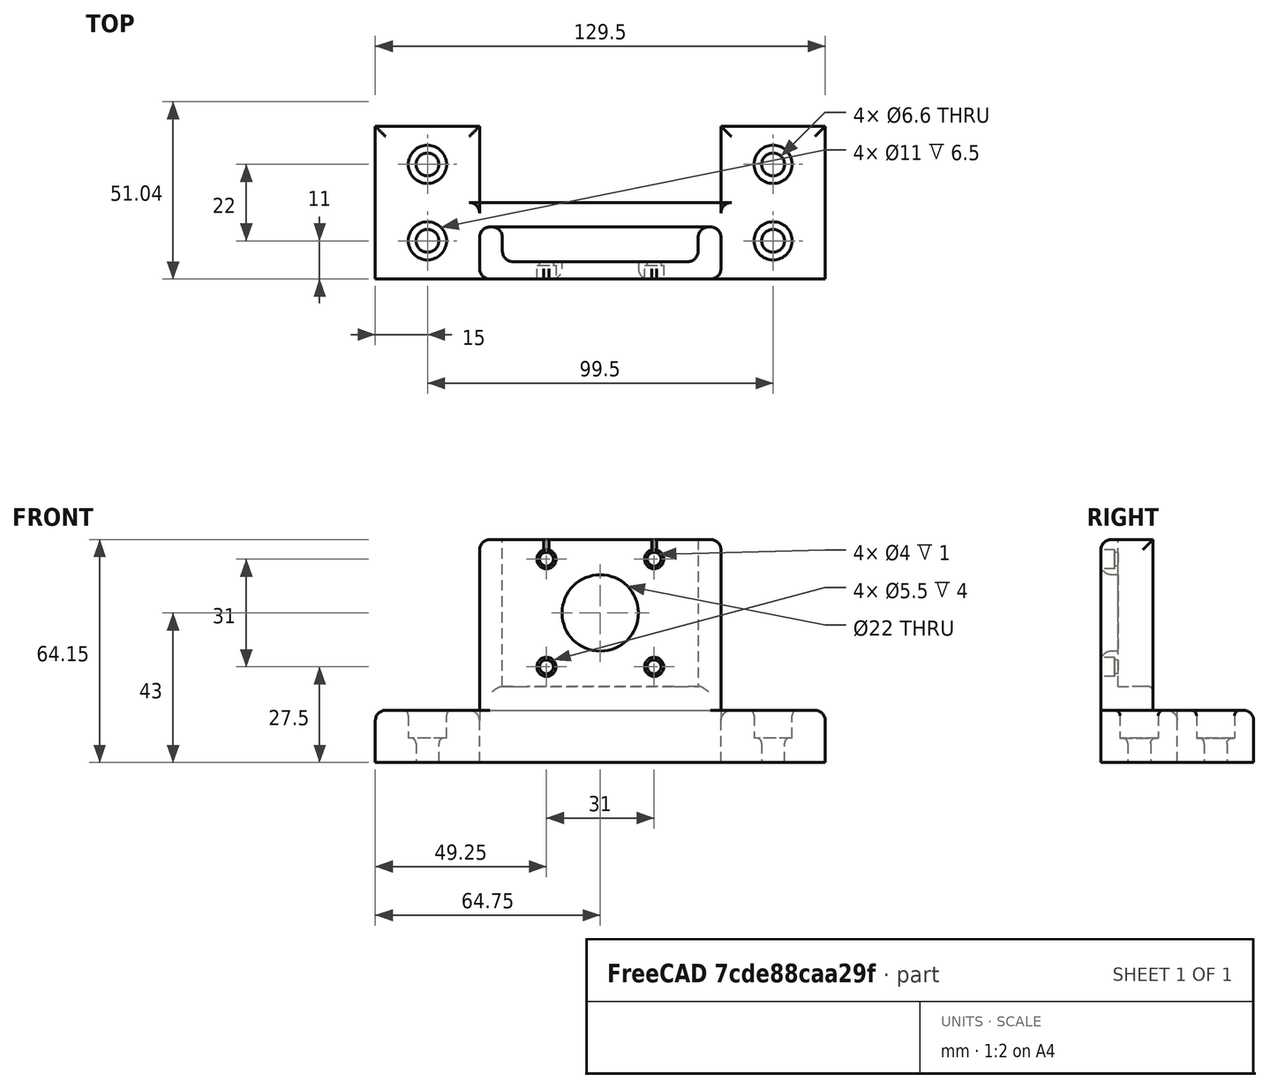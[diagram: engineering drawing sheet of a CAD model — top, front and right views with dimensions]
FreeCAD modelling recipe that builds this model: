
FCSTD DOCUMENT  (FreeCAD 1.0R1.0.0)
Label: CrossTableMount02
License: All rights reserved
LicenseURL: http://en.wikipedia.org/wiki/All_rights_reserved
objects: Part::Box×8, Part::Cylinder×8, Part::MultiFuse×7, Part::Fillet×5, Spreadsheet::Sheet×1, Part::Feature×1, Part::Compound×1, Part::Cut×1
note: 31 computed .brp shape members not serialized (recipe doc carries the construction recipe); baked Part::Feature solids carry a one-line shape summary decoded from their .brp

FEATURE [Spreadsheet::Sheet] Spreadsheet
  cells = A2='Profile width; B2(profilewidth)=30; E2='Screw threaded hole length; F2(screw_threadlen)==screwlen - 9; A3='Slot spacing; B3(slotspacing)=99.5; E3='Screw head hole len; F3(screw_headlen)==max(screw_headheight; 15 - screw_threadlen); A4='Screw hole dia; B4(screw_holedia)=6.6; A5='Screw head dia; B5(screw_headdia)=11; C5='10 but make sure it fits; A6='Screw height; B6(screwlen)=16; A7='Screw head height; B7(screw_headheight)=7; A8='Motor vertical offset; B8(motor_off_v)=43
FEATURE [Part::Box] Box  label="Cube"
  AttacherType = Attacher::AttachEngine3D
  Height = 15
  Length = 129.5
  Placement = pos=(-64.75,0,0) rot=(0,0,1;0rad)
  Width = 22
  expr: .Placement.Base.x = -(Spreadsheet.slotspacing + Spreadsheet.profilewidth) / 2
  expr: Height = Spreadsheet.screw_threadlen + Spreadsheet.screw_headlen
  expr: Length = Spreadsheet.slotspacing + Spreadsheet.profilewidth
  expr: Width = 2 * Spreadsheet.screw_headdia
FEATURE [Part::Cylinder] Cylinder
  Angle = 360
  AttacherType = Attacher::AttachEngine3D
  FirstAngle = 0
  Height = 7
  Radius = 3.3
  SecondAngle = 0
  expr: Height = Spreadsheet.screw_threadlen
  expr: Radius = Spreadsheet.screw_holedia / 2
FEATURE [Part::Cylinder] Cylinder001
  Angle = 360
  AttacherType = Attacher::AttachEngine3D
  FirstAngle = 0
  Height = 8
  Placement = pos=(0,0,7) rot=(0,0,1;0rad)
  Radius = 5.5
  SecondAngle = 0
  expr: .Placement.Base.z = Spreadsheet.screw_threadlen
  expr: Height = Spreadsheet.screw_headlen
  expr: Radius = Spreadsheet.screw_headdia / 2
FEATURE [Part::MultiFuse] Fusion
  Placement = pos=(49.75,11,0) rot=(0,0,1;0rad)
  Shapes = -> [Cylinder,Cylinder001]
  expr: .Placement.Base.x = Spreadsheet.slotspacing / 2
  expr: .Placement.Base.y = Spreadsheet.screw_headdia
FEATURE [Part::Cylinder] Cylinder002
  Angle = 360
  AttacherType = Attacher::AttachEngine3D
  FirstAngle = 0
  Height = 7
  Radius = 3.3
  SecondAngle = 0
  expr: Height = Spreadsheet.screw_threadlen
  expr: Radius = Spreadsheet.screw_holedia / 2
FEATURE [Part::Cylinder] Cylinder003
  Angle = 360
  AttacherType = Attacher::AttachEngine3D
  FirstAngle = 0
  Height = 8
  Placement = pos=(0,0,7) rot=(0,0,1;0rad)
  Radius = 5.5
  SecondAngle = 0
  expr: .Placement.Base.z = Spreadsheet.screw_threadlen
  expr: Height = Spreadsheet.screw_headlen
  expr: Radius = Spreadsheet.screw_headdia / 2
FEATURE [Part::MultiFuse] Fusion001
  Placement = pos=(-49.75,11,0) rot=(0,0,1;0rad)
  Shapes = -> [Cylinder002,Cylinder003]
  expr: .Placement.Base.x = -Spreadsheet.slotspacing / 2
  expr: .Placement.Base.y = Spreadsheet.screw_headdia
FEATURE [Part::Box] Box001  label="Cube001"
  AttacherType = Attacher::AttachEngine3D
  Height = 15
  Length = 30
  Placement = pos=(34.75,0,0) rot=(0,0,1;0rad)
  Width = 44
  expr: .Placement.Base.x = (Spreadsheet.slotspacing - Spreadsheet.profilewidth) / 2
  expr: Height = Spreadsheet.screw_threadlen + Spreadsheet.screw_headlen
  expr: Length = Spreadsheet.profilewidth
  expr: Width = 4 * Spreadsheet.screw_headdia
FEATURE [Part::Box] Box002  label="Cube002"
  AttacherType = Attacher::AttachEngine3D
  Height = 15
  Length = 30
  Placement = pos=(-64.75,0,0) rot=(0,0,1;0rad)
  Width = 44
  expr: .Placement.Base.x = -(Spreadsheet.slotspacing + Spreadsheet.profilewidth) / 2
  expr: Height = Spreadsheet.screw_threadlen + Spreadsheet.screw_headlen
  expr: Length = Spreadsheet.profilewidth
  expr: Width = 4 * Spreadsheet.screw_headdia
FEATURE [Part::Cylinder] Cylinder004
  Angle = 360
  AttacherType = Attacher::AttachEngine3D
  FirstAngle = 0
  Height = 7
  Radius = 3.3
  SecondAngle = 0
  expr: Height = Spreadsheet.screw_threadlen
  expr: Radius = Spreadsheet.screw_holedia / 2
FEATURE [Part::Cylinder] Cylinder005
  Angle = 360
  AttacherType = Attacher::AttachEngine3D
  FirstAngle = 0
  Height = 8
  Placement = pos=(0,0,7) rot=(0,0,1;0rad)
  Radius = 5.5
  SecondAngle = 0
  expr: .Placement.Base.z = Spreadsheet.screw_threadlen
  expr: Height = Spreadsheet.screw_headlen
  expr: Radius = Spreadsheet.screw_headdia / 2
FEATURE [Part::Cylinder] Cylinder006
  Angle = 360
  AttacherType = Attacher::AttachEngine3D
  FirstAngle = 0
  Height = 7
  Radius = 3.3
  SecondAngle = 0
  expr: Height = Spreadsheet.screw_threadlen
  expr: Radius = Spreadsheet.screw_holedia / 2
FEATURE [Part::Cylinder] Cylinder007
  Angle = 360
  AttacherType = Attacher::AttachEngine3D
  FirstAngle = 0
  Height = 8
  Placement = pos=(0,0,7) rot=(0,0,1;0rad)
  Radius = 5.5
  SecondAngle = 0
  expr: .Placement.Base.z = Spreadsheet.screw_threadlen
  expr: Height = Spreadsheet.screw_headlen
  expr: Radius = Spreadsheet.screw_headdia / 2
FEATURE [Part::MultiFuse] Fusion002
  Placement = pos=(49.75,33,0) rot=(0,0,1;0rad)
  Shapes = -> [Cylinder004,Cylinder005]
  expr: .Placement.Base.x = Spreadsheet.slotspacing / 2
  expr: .Placement.Base.y = 3 * Spreadsheet.screw_headdia
FEATURE [Part::MultiFuse] Fusion003
  Placement = pos=(-49.75,33,0) rot=(0,0,1;0rad)
  Shapes = -> [Cylinder006,Cylinder007]
  expr: .Placement.Base.x = -Spreadsheet.slotspacing / 2
  expr: .Placement.Base.y = 3 * Spreadsheet.screw_headdia
FEATURE [Part::MultiFuse] Fusion004
  Shapes = -> [Box001,Box002,Box]
FEATURE [Part::Feature] Cut003_solid  label="MountplateTemplate"
  Placement = pos=(0,0,0) rot=(1,0,0;1.5708rad)
  shape: bbox 42.3 x 5 x 42.3 mm, 19 faces (baked)
FEATURE [Part::Compound] Compound
  Links = -> [Cut003_solid]
  Placement = pos=(0,5,43) rot=(0,0,1;3.14159rad)
  expr: .Placement.Base.z = Spreadsheet.motor_off_v
FEATURE [Part::Box] Box003  label="Cube003"
  AttacherType = Attacher::AttachEngine3D
  Height = 21.85
  Length = 69.5
  Placement = pos=(-34.75,0,0) rot=(0,0,1;0rad)
  Width = 15
  expr: .Placement.Base.x = -(Spreadsheet.slotspacing - Spreadsheet.profilewidth) / 2
  expr: Height = Spreadsheet.motor_off_v - 42.3 / 2
  expr: Length = Spreadsheet.slotspacing - Spreadsheet.profilewidth
FEATURE [Part::Box] Box004  label="Cube004"
  AttacherType = Attacher::AttachEngine3D
  Height = 64.15
  Length = 13.6
  Placement = pos=(-34.75,0,0) rot=(0,0,1;0rad)
  Width = 5
  expr: .Placement.Base.x = -(Spreadsheet.slotspacing - Spreadsheet.profilewidth) / 2
  expr: Height = Spreadsheet.motor_off_v + 42.3 / 2
  expr: Length = (Spreadsheet.slotspacing - Spreadsheet.profilewidth - 42.3) / 2
FEATURE [Part::Box] Box005  label="Cube005"
  AttacherType = Attacher::AttachEngine3D
  Height = 64.15
  Length = 6.575
  Placement = pos=(28.175,0,0) rot=(0,0,1;0rad)
  Width = 15
  expr: .Placement.Base.x = (Spreadsheet.slotspacing - Spreadsheet.profilewidth) / 2 - (Spreadsheet.slotspacing - Spreadsheet.profilewidth - 43.2) / 4
  expr: Height = Spreadsheet.motor_off_v + 42.3 / 2
  expr: Length = (Spreadsheet.slotspacing - Spreadsheet.profilewidth - 43.2) / 4
FEATURE [Part::Box] Box006  label="Cube006"
  AttacherType = Attacher::AttachEngine3D
  Height = 64.15
  Length = 13.6
  Placement = pos=(21.15,0,0) rot=(0,0,1;0rad)
  Width = 5
  expr: .Placement.Base.x = (Spreadsheet.slotspacing - Spreadsheet.profilewidth) / 2 - (Spreadsheet.slotspacing - Spreadsheet.profilewidth - 42.3) / 2
  expr: Height = Spreadsheet.motor_off_v + 42.3 / 2
  expr: Length = (Spreadsheet.slotspacing - Spreadsheet.profilewidth - 42.3) / 2
FEATURE [Part::Box] Box007  label="Cube007"
  AttacherType = Attacher::AttachEngine3D
  Height = 64.15
  Length = 6.575
  Placement = pos=(-34.75,0,0) rot=(0,0,1;0rad)
  Width = 15
  expr: .Placement.Base.x = -(Spreadsheet.slotspacing - Spreadsheet.profilewidth) / 2
  expr: Height = Spreadsheet.motor_off_v + 42.3 / 2
  expr: Length = (Spreadsheet.slotspacing - Spreadsheet.profilewidth - 43.2) / 4
FEATURE [Part::MultiFuse] Fusion005
  Shapes = -> [Box007,Box006,Box005,Box004,Box003,Compound,Fusion004]
FEATURE [Part::MultiFuse] Fusion006
  Shapes = -> [Fusion003,Fusion002,Fusion001,Fusion]
FEATURE [Part::Cut] Cut
  Base = -> Fusion005
  Tool = -> Fusion006
FEATURE [Part::Fillet] Fillet
  Base = -> Cut
  EdgeLinks = -> Cut [Edge33,Edge100,Edge108,Edge111,Edge154,Edge155,Edge165,Edge167,Edge174,Edge189,Edge194]
  Edges = 11 edges r=3: [Edge33,Edge100,Edge108,Edge111,Edge154,Edge155,Edge165,Edge167,Edge174,Edge189,Edge194]
FEATURE [Part::Fillet] Fillet001
  Base = -> Fillet
  EdgeLinks = -> Fillet [Edge17,Edge50,Edge94,Edge107,Edge173,Edge180,Edge249,Edge272]
  Edges = 8 edges r=1.5: [Edge17,Edge50,Edge94,Edge107,Edge173,Edge180,Edge249,Edge272]
FEATURE [Part::Fillet] Fillet002
  Base = -> Fillet001
  EdgeLinks = -> Fillet001 [Edge9,Edge31,Edge37,Edge38,Edge39,Edge73,Edge142,Edge143,Edge144]
  Edges = 9 edges r=3: [Edge9,Edge31,Edge37,Edge38,Edge39,Edge73,Edge142,Edge143,Edge144]
FEATURE [Part::Fillet] Fillet003
  Base = -> Fillet002
  EdgeLinks = -> Fillet002 [Edge89]
  Edges = 1 edges r=1.5: [Edge89]
FEATURE [Part::Fillet] Fillet004
  Base = -> Fillet003
  EdgeLinks = -> Fillet003 [Edge171]
  Edges = 1 edges r=3: [Edge171]
